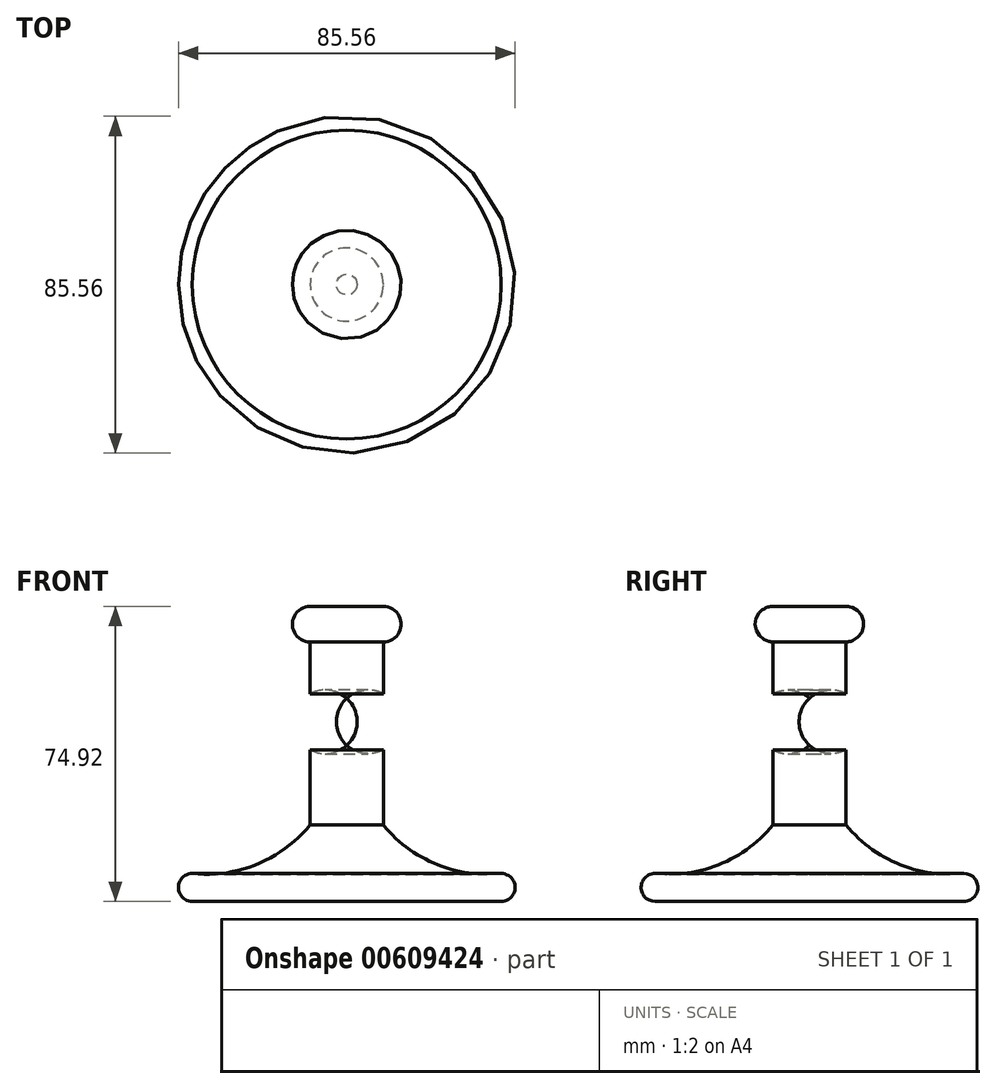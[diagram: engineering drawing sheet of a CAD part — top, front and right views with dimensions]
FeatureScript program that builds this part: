
annotation { "Feature Type Name" : "Feature", "Feature Type Description" : "" }
export const myFeature = defineFeature(function(context is Context, id is Id, definition is map)
    precondition{}
    {
        {
            var Q0;
            Q0=qCreatedBy(makeId("Front.planeOp"),FACE);
            var sketch = newSketch(context, id + "F0", { "sketchPlane" : qUnion([Q0])});
            skLineSegment(sketch, "E0", {"start": v(0, 0) * mm, "end": v(39.24, 0) * mm});
            skLineSegment(sketch, "E1", {"start": v(0, 0) * mm, "end": v(0, 74.92) * mm});
            skLineSegment(sketch, "E2", {"start": v(0, 74.92) * mm, "end": v(9.3, 74.92) * mm});
            skArc(sketch, "E3", {"start": v(9.3, 65.91) * mm, "mid": v(13.8, 70.42) * mm, "end": v(9.3, 74.92) * mm});
            skLineSegment(sketch, "E4", {"start": v(9.3, 65.91) * mm, "end": v(9.3, 52.72) * mm});
            skArc(sketch, "E5", {"start": v(9.3, 38.48) * mm, "mid": v(13.55, 45.6) * mm, "end": v(9.3, 52.72) * mm});
            skLineSegment(sketch, "E6", {"start": v(9.3, 38.48) * mm, "end": v(9.3, 19.43) * mm});
            skArc(sketch, "E7", {"start": v(39.24, 0) * mm, "mid": v(42.78, 3.54) * mm, "end": v(39.24, 7.07) * mm});
            skArc(sketch, "E8", {"start": v(9.3, 19.43) * mm, "mid": v(22.7, 9.46) * mm, "end": v(39.24, 7.07) * mm});
            skSolve(sketch);
        }
        {
            var Q0;
            Q0=makeQuery(id+"F0.imprint","IMPRINT",FACE,{"disambiguationData":[TD([[makeQuery(id+"F0.imprint","IMPRINT",EDGE,{"derivedFrom":sQuery(id+"F0.wireOp",EDGE,"E0")}),1.0]])]});
            var Q1;
            Q1=sQuery(id+"F0.wireOp",EDGE,"E1");
            revolve(context, id + "F1", {"entities" : qUnion([Q0]), "axis" : qUnion([Q1]), "revolveType" : RevolveType.FULL});
        }
    });
